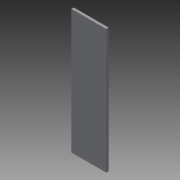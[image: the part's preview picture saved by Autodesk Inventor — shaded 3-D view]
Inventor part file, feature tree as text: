
AUTODESK INVENTOR PART (.ipt)
format: ipt  version: 2015 SP1 (Build 190203100, 203)  size: 68,608 bytes
history: native  units: in
note: dims shown in document units (in); Inventor stores cm internally (conversion verified against a paired STEP export)
features: extrude x1, sketch x1
ambient origin geometry x8: Origin, YZ Plane, XZ Plane, XY Plane, X Axis, Y Axis, Z Axis, Center Point
bodies: Solid1 (feature_tree)
feature tree (2):
  extrude  "Extrusion1"  Depth=1.1024in
  sketch  "Sketch1"  dims[d0=3.937in d1=1.1024in d2=0.0787in d3=0.0in]
